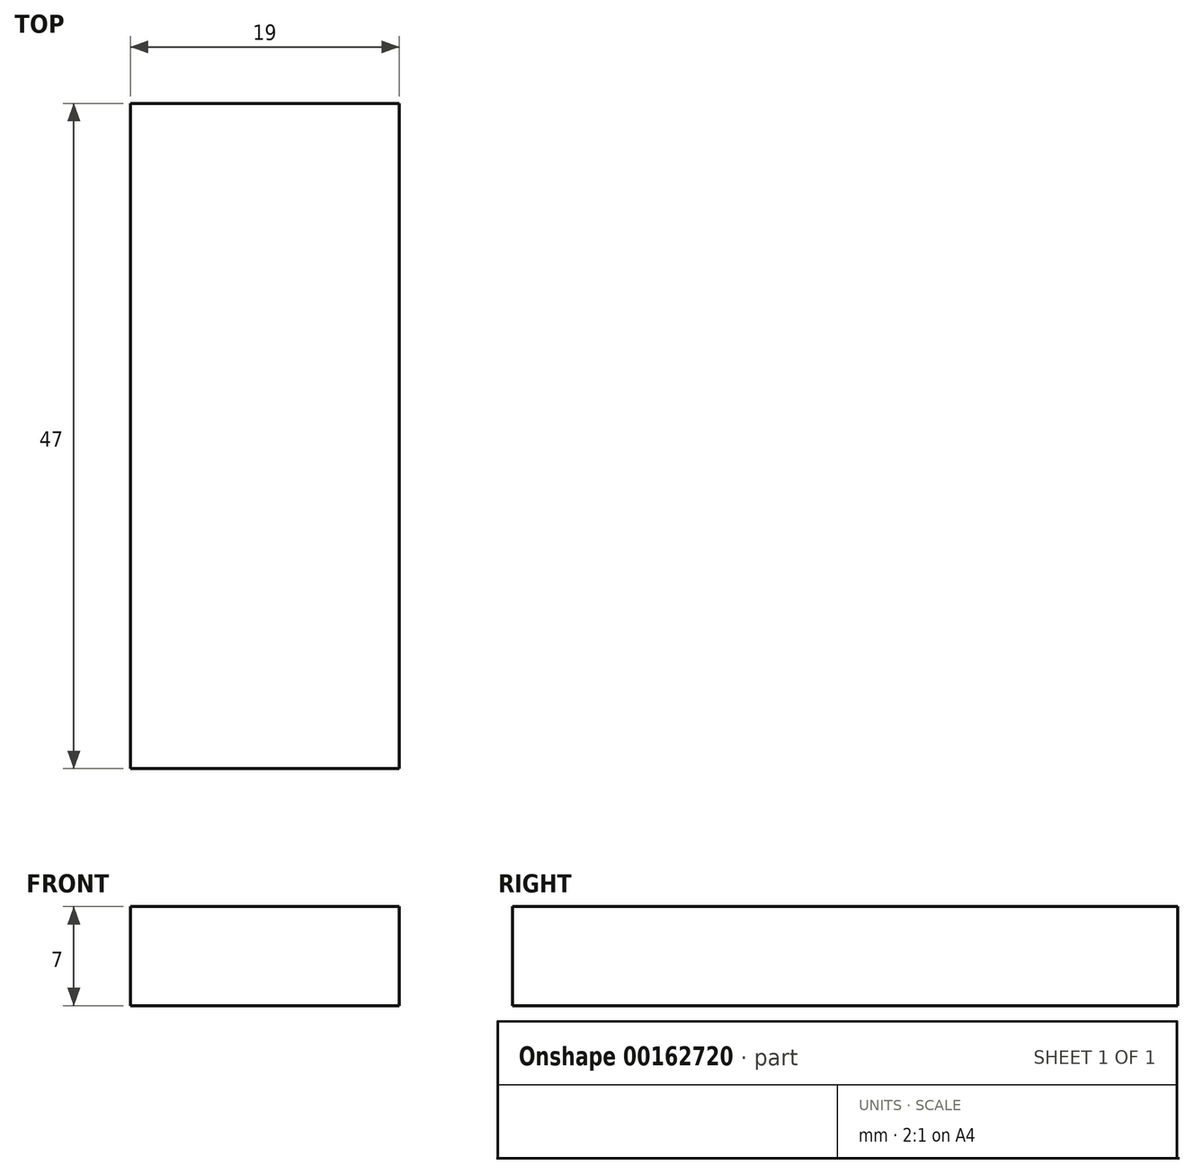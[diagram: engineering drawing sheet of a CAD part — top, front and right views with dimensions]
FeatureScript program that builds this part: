
annotation { "Feature Type Name" : "Feature", "Feature Type Description" : "" }
export const myFeature = defineFeature(function(context is Context, id is Id, definition is map)
    precondition{}
    {
        {
            var Q0;
            Q0=qCreatedBy(makeId("Top.planeOp"),FACE);
            var sketch = newSketch(context, id + "F0", { "sketchPlane" : qUnion([Q0])});
            skLineSegment(sketch, "E0.bottom", {"start": v(9.5, 23.5) * mm, "end": v(-9.5, 23.5) * mm});
            skLineSegment(sketch, "E0.top", {"start": v(9.5, -23.5) * mm, "end": v(-9.5, -23.5) * mm});
            skLineSegment(sketch, "E0.left", {"start": v(9.5, 23.5) * mm, "end": v(9.5, -23.5) * mm});
            skLineSegment(sketch, "E0.right", {"start": v(-9.5, 23.5) * mm, "end": v(-9.5, -23.5) * mm});
            skPoint(sketch, "E0.middle", {"position": v(0, 0) * mm});
            skSolve(sketch);
        }
        {
            var Q0;
            Q0=qSketchRegion(id+"F0",true);
            extrude(context, id + "F1", {"entities" : qUnion([Q0]), "depth" : 7 * mm});
        }
    });
